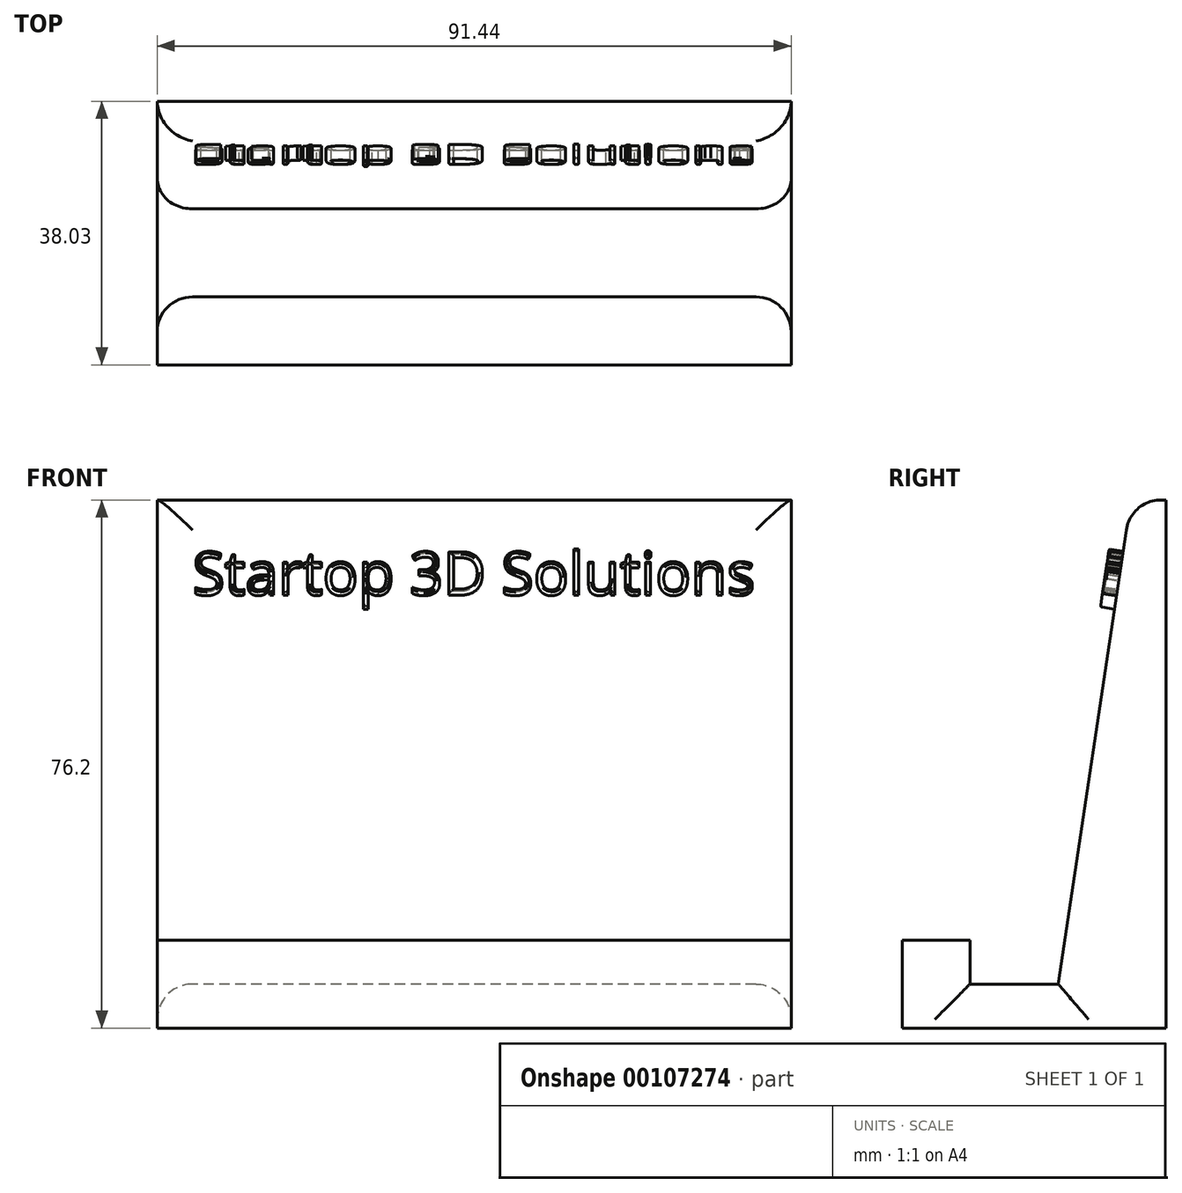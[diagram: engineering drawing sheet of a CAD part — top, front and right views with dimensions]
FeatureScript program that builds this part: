
annotation { "Feature Type Name" : "Feature", "Feature Type Description" : "" }
export const myFeature = defineFeature(function(context is Context, id is Id, definition is map)
    precondition{}
    {
        {
            var Q0;
            Q0=qCreatedBy(makeId("Right.planeOp"),FACE);
            var sketch = newSketch(context, id + "F0", { "sketchPlane" : qUnion([Q0])});
            skLineSegment(sketch, "E0", {"start": v(0, 0) * mm, "end": v(38.03, 0) * mm});
            skLineSegment(sketch, "E1", {"start": v(38.03, 0) * mm, "end": v(38.03, 76.2) * mm});
            skLineSegment(sketch, "E2", {"start": v(38.03, 76.2) * mm, "end": v(32.95, 76.2) * mm});
            skLineSegment(sketch, "E3", {"start": v(32.95, 76.2) * mm, "end": v(22.5, 6.35) * mm});
            skLineSegment(sketch, "E4", {"start": v(22.5, 6.35) * mm, "end": v(9.8, 6.35) * mm});
            skLineSegment(sketch, "E5", {"start": v(9.8, 6.35) * mm, "end": v(9.8, 12.7) * mm});
            skLineSegment(sketch, "E6", {"start": v(9.8, 12.7) * mm, "end": v(0, 12.7) * mm});
            skLineSegment(sketch, "E7", {"start": v(0, 12.7) * mm, "end": v(0, 0) * mm});
            skSolve(sketch);
        }
        {
            var Q0;
            Q0=makeQuery(id+"F0.imprint","IMPRINT",FACE,{"disambiguationData":[TD([[makeQuery(id+"F0.imprint","IMPRINT",EDGE,{"derivedFrom":sQuery(id+"F0.wireOp",EDGE,"E0")}),1.0]])]});
            extrude(context, id + "F1", {"entities" : qUnion([Q0]), "depth" : 91.44 * mm});
        }
        {
            var Q0;
            Q0=makeQuery(id+"F1.opExtrude","SWEPT_EDGE",EDGE,{"disambiguationData":[OSD([sQuery(id+"F0.wireOp",EDGE,"E2"),sQuery(id+"F0.wireOp",EDGE,"E3")])]});
            var Q1;
            Q1=makeQuery(id+"F1.opExtrude","CAP_EDGE",EDGE,{"disambiguationData":[OSD([sQuery(id+"F0.wireOp",EDGE,"E3")])],"isStart":false});
            var Q2;
            Q2=makeQuery(id+"F1.opExtrude","CAP_EDGE",EDGE,{"disambiguationData":[OSD([sQuery(id+"F0.wireOp",EDGE,"E3")])],"isStart":true});
            var Q3;
            Q3=makeQuery(id+"F1.opExtrude","CAP_EDGE",EDGE,{"disambiguationData":[OSD([sQuery(id+"F0.wireOp",EDGE,"E4")])],"isStart":false});
            var Q4;
            Q4=makeQuery(id+"F1.opExtrude","CAP_EDGE",EDGE,{"disambiguationData":[OSD([sQuery(id+"F0.wireOp",EDGE,"E4")])],"isStart":true});
            var Q5;
            Q5=makeQuery(id+"F1.opExtrude","CAP_EDGE",EDGE,{"disambiguationData":[OSD([sQuery(id+"F0.wireOp",EDGE,"E5")])],"isStart":true});
            var Q6;
            Q6=makeQuery(id+"F1.opExtrude","CAP_EDGE",EDGE,{"disambiguationData":[OSD([sQuery(id+"F0.wireOp",EDGE,"E5")])],"isStart":false});
            fillet(context, id + "F2", {"entities" : qUnion([Q0, Q1, Q2, Q3, Q4, Q5, Q6]), "radius" : 5.08 * mm, "tangentPropagation" : true, "allowEdgeOverflow" : false});
        }
        {
            var Q0;
            Q0=makeQuery(id+"F1.opExtrude","SWEPT_FACE",FACE,{"disambiguationData":[OSD([sQuery(id+"F0.wireOp",EDGE,"E3")])]});
            var sketch = newSketch(context, id + "F3", { "sketchPlane" : qUnion([Q0])});
            skText(sketch, "E8", { "text": "Startop 3D Solutions", "fontName": "OpenSans-Regular.ttf"});
            const initialGuessF3  = {"E8": [0.00508, 0.06635, 1, 0, 0.0061]};
            skSetInitialGuess(sketch, initialGuessF3);
            skSolve(sketch);
        }
        {
            var Q0;
            Q0=qSketchRegion(id+"F3",true);
            extrude(context, id + "F4", {"entities" : qUnion([Q0]), "operationType" : NewBodyOperationType.ADD, "depth" : 2.03 * mm});
        }
        {
            var Q0;
            Q0=makeQuery(id+"F4.opExtrude","CAP_FACE",FACE,{"disambiguationData":[OSD([sQuery(id+"F3.wireOp",EDGE,"E8.sketch_text.stroke-0"),sQuery(id+"F3.wireOp",EDGE,"E8.sketch_text.stroke-1"),sQuery(id+"F3.wireOp",EDGE,"E8.sketch_text.stroke-2"),sQuery(id+"F3.wireOp",EDGE,"E8.sketch_text.stroke-3"),sQuery(id+"F3.wireOp",EDGE,"E8.sketch_text.stroke-4"),sQuery(id+"F3.wireOp",EDGE,"E8.sketch_text.stroke-5"),sQuery(id+"F3.wireOp",EDGE,"E8.sketch_text.stroke-6"),sQuery(id+"F3.wireOp",EDGE,"E8.sketch_text.stroke-7"),sQuery(id+"F3.wireOp",EDGE,"E8.sketch_text.stroke-8"),sQuery(id+"F3.wireOp",EDGE,"E8.sketch_text.stroke-9"),sQuery(id+"F3.wireOp",EDGE,"E8.sketch_text.stroke-10"),sQuery(id+"F3.wireOp",EDGE,"E8.sketch_text.stroke-11"),sQuery(id+"F3.wireOp",EDGE,"E8.sketch_text.stroke-12"),sQuery(id+"F3.wireOp",EDGE,"E8.sketch_text.stroke-13"),sQuery(id+"F3.wireOp",EDGE,"E8.sketch_text.stroke-14"),sQuery(id+"F3.wireOp",EDGE,"E8.sketch_text.stroke-15"),sQuery(id+"F3.wireOp",EDGE,"E8.sketch_text.stroke-16"),sQuery(id+"F3.wireOp",EDGE,"E8.sketch_text.stroke-17"),sQuery(id+"F3.wireOp",EDGE,"E8.sketch_text.stroke-18"),sQuery(id+"F3.wireOp",EDGE,"E8.sketch_text.stroke-19"),sQuery(id+"F3.wireOp",EDGE,"E8.sketch_text.stroke-20"),sQuery(id+"F3.wireOp",EDGE,"E8.sketch_text.stroke-21"),sQuery(id+"F3.wireOp",EDGE,"E8.sketch_text.stroke-22"),sQuery(id+"F3.wireOp",EDGE,"E8.sketch_text.stroke-23"),sQuery(id+"F3.wireOp",EDGE,"E8.sketch_text.stroke-24")])],"isStart":false});
            var Q1;
            Q1=makeQuery(id+"F4.opExtrude","CAP_FACE",FACE,{"disambiguationData":[OSD([sQuery(id+"F3.wireOp",EDGE,"E8.sketch_text.stroke-25"),sQuery(id+"F3.wireOp",EDGE,"E8.sketch_text.stroke-26"),sQuery(id+"F3.wireOp",EDGE,"E8.sketch_text.stroke-27"),sQuery(id+"F3.wireOp",EDGE,"E8.sketch_text.stroke-28"),sQuery(id+"F3.wireOp",EDGE,"E8.sketch_text.stroke-29"),sQuery(id+"F3.wireOp",EDGE,"E8.sketch_text.stroke-30"),sQuery(id+"F3.wireOp",EDGE,"E8.sketch_text.stroke-31"),sQuery(id+"F3.wireOp",EDGE,"E8.sketch_text.stroke-32"),sQuery(id+"F3.wireOp",EDGE,"E8.sketch_text.stroke-33"),sQuery(id+"F3.wireOp",EDGE,"E8.sketch_text.stroke-34"),sQuery(id+"F3.wireOp",EDGE,"E8.sketch_text.stroke-35"),sQuery(id+"F3.wireOp",EDGE,"E8.sketch_text.stroke-36"),sQuery(id+"F3.wireOp",EDGE,"E8.sketch_text.stroke-37"),sQuery(id+"F3.wireOp",EDGE,"E8.sketch_text.stroke-38"),sQuery(id+"F3.wireOp",EDGE,"E8.sketch_text.stroke-39"),sQuery(id+"F3.wireOp",EDGE,"E8.sketch_text.stroke-40"),sQuery(id+"F3.wireOp",EDGE,"E8.sketch_text.stroke-41"),sQuery(id+"F3.wireOp",EDGE,"E8.sketch_text.stroke-42"),sQuery(id+"F3.wireOp",EDGE,"E8.sketch_text.stroke-43")])],"isStart":false});
            var Q2;
            Q2=makeQuery(id+"F4.opExtrude","CAP_FACE",FACE,{"disambiguationData":[OSD([sQuery(id+"F3.wireOp",EDGE,"E8.sketch_text.stroke-44"),sQuery(id+"F3.wireOp",EDGE,"E8.sketch_text.stroke-45"),sQuery(id+"F3.wireOp",EDGE,"E8.sketch_text.stroke-46"),sQuery(id+"F3.wireOp",EDGE,"E8.sketch_text.stroke-47"),sQuery(id+"F3.wireOp",EDGE,"E8.sketch_text.stroke-48"),sQuery(id+"F3.wireOp",EDGE,"E8.sketch_text.stroke-49"),sQuery(id+"F3.wireOp",EDGE,"E8.sketch_text.stroke-50"),sQuery(id+"F3.wireOp",EDGE,"E8.sketch_text.stroke-51"),sQuery(id+"F3.wireOp",EDGE,"E8.sketch_text.stroke-52"),sQuery(id+"F3.wireOp",EDGE,"E8.sketch_text.stroke-53"),sQuery(id+"F3.wireOp",EDGE,"E8.sketch_text.stroke-54"),sQuery(id+"F3.wireOp",EDGE,"E8.sketch_text.stroke-55"),sQuery(id+"F3.wireOp",EDGE,"E8.sketch_text.stroke-56"),sQuery(id+"F3.wireOp",EDGE,"E8.sketch_text.stroke-57"),sQuery(id+"F3.wireOp",EDGE,"E8.sketch_text.stroke-58"),sQuery(id+"F3.wireOp",EDGE,"E8.sketch_text.stroke-59"),sQuery(id+"F3.wireOp",EDGE,"E8.sketch_text.stroke-60"),sQuery(id+"F3.wireOp",EDGE,"E8.sketch_text.stroke-61"),sQuery(id+"F3.wireOp",EDGE,"E8.sketch_text.stroke-62"),sQuery(id+"F3.wireOp",EDGE,"E8.sketch_text.stroke-63"),sQuery(id+"F3.wireOp",EDGE,"E8.sketch_text.stroke-64"),sQuery(id+"F3.wireOp",EDGE,"E8.sketch_text.stroke-65"),sQuery(id+"F3.wireOp",EDGE,"E8.sketch_text.stroke-66"),sQuery(id+"F3.wireOp",EDGE,"E8.sketch_text.stroke-67"),sQuery(id+"F3.wireOp",EDGE,"E8.sketch_text.stroke-68"),sQuery(id+"F3.wireOp",EDGE,"E8.sketch_text.stroke-69"),sQuery(id+"F3.wireOp",EDGE,"E8.sketch_text.stroke-70")])],"isStart":false});
            var Q3;
            Q3=makeQuery(id+"F4.opExtrude","CAP_FACE",FACE,{"disambiguationData":[OSD([sQuery(id+"F3.wireOp",EDGE,"E8.sketch_text.stroke-71"),sQuery(id+"F3.wireOp",EDGE,"E8.sketch_text.stroke-72"),sQuery(id+"F3.wireOp",EDGE,"E8.sketch_text.stroke-73"),sQuery(id+"F3.wireOp",EDGE,"E8.sketch_text.stroke-74"),sQuery(id+"F3.wireOp",EDGE,"E8.sketch_text.stroke-75"),sQuery(id+"F3.wireOp",EDGE,"E8.sketch_text.stroke-76"),sQuery(id+"F3.wireOp",EDGE,"E8.sketch_text.stroke-77"),sQuery(id+"F3.wireOp",EDGE,"E8.sketch_text.stroke-78"),sQuery(id+"F3.wireOp",EDGE,"E8.sketch_text.stroke-79"),sQuery(id+"F3.wireOp",EDGE,"E8.sketch_text.stroke-80"),sQuery(id+"F3.wireOp",EDGE,"E8.sketch_text.stroke-81"),sQuery(id+"F3.wireOp",EDGE,"E8.sketch_text.stroke-82"),sQuery(id+"F3.wireOp",EDGE,"E8.sketch_text.stroke-83")])],"isStart":false});
            var Q4;
            Q4=makeQuery(id+"F4.opExtrude","CAP_FACE",FACE,{"disambiguationData":[OSD([sQuery(id+"F3.wireOp",EDGE,"E8.sketch_text.stroke-84"),sQuery(id+"F3.wireOp",EDGE,"E8.sketch_text.stroke-85"),sQuery(id+"F3.wireOp",EDGE,"E8.sketch_text.stroke-86"),sQuery(id+"F3.wireOp",EDGE,"E8.sketch_text.stroke-87"),sQuery(id+"F3.wireOp",EDGE,"E8.sketch_text.stroke-88"),sQuery(id+"F3.wireOp",EDGE,"E8.sketch_text.stroke-89"),sQuery(id+"F3.wireOp",EDGE,"E8.sketch_text.stroke-90"),sQuery(id+"F3.wireOp",EDGE,"E8.sketch_text.stroke-91"),sQuery(id+"F3.wireOp",EDGE,"E8.sketch_text.stroke-92"),sQuery(id+"F3.wireOp",EDGE,"E8.sketch_text.stroke-93"),sQuery(id+"F3.wireOp",EDGE,"E8.sketch_text.stroke-94"),sQuery(id+"F3.wireOp",EDGE,"E8.sketch_text.stroke-95"),sQuery(id+"F3.wireOp",EDGE,"E8.sketch_text.stroke-96"),sQuery(id+"F3.wireOp",EDGE,"E8.sketch_text.stroke-97"),sQuery(id+"F3.wireOp",EDGE,"E8.sketch_text.stroke-98"),sQuery(id+"F3.wireOp",EDGE,"E8.sketch_text.stroke-99"),sQuery(id+"F3.wireOp",EDGE,"E8.sketch_text.stroke-100"),sQuery(id+"F3.wireOp",EDGE,"E8.sketch_text.stroke-101"),sQuery(id+"F3.wireOp",EDGE,"E8.sketch_text.stroke-102")])],"isStart":false});
            var Q5;
            Q5=makeQuery(id+"F4.opExtrude","CAP_FACE",FACE,{"disambiguationData":[OSD([sQuery(id+"F3.wireOp",EDGE,"E8.sketch_text.stroke-103"),sQuery(id+"F3.wireOp",EDGE,"E8.sketch_text.stroke-104"),sQuery(id+"F3.wireOp",EDGE,"E8.sketch_text.stroke-105"),sQuery(id+"F3.wireOp",EDGE,"E8.sketch_text.stroke-106"),sQuery(id+"F3.wireOp",EDGE,"E8.sketch_text.stroke-107"),sQuery(id+"F3.wireOp",EDGE,"E8.sketch_text.stroke-108"),sQuery(id+"F3.wireOp",EDGE,"E8.sketch_text.stroke-109"),sQuery(id+"F3.wireOp",EDGE,"E8.sketch_text.stroke-110"),sQuery(id+"F3.wireOp",EDGE,"E8.sketch_text.stroke-111"),sQuery(id+"F3.wireOp",EDGE,"E8.sketch_text.stroke-112"),sQuery(id+"F3.wireOp",EDGE,"E8.sketch_text.stroke-113"),sQuery(id+"F3.wireOp",EDGE,"E8.sketch_text.stroke-114"),sQuery(id+"F3.wireOp",EDGE,"E8.sketch_text.stroke-115"),sQuery(id+"F3.wireOp",EDGE,"E8.sketch_text.stroke-116"),sQuery(id+"F3.wireOp",EDGE,"E8.sketch_text.stroke-117"),sQuery(id+"F3.wireOp",EDGE,"E8.sketch_text.stroke-118"),sQuery(id+"F3.wireOp",EDGE,"E8.sketch_text.stroke-119")])],"isStart":false});
            var Q6;
            Q6=makeQuery(id+"F4.opExtrude","CAP_FACE",FACE,{"disambiguationData":[OSD([sQuery(id+"F3.wireOp",EDGE,"E8.sketch_text.stroke-120"),sQuery(id+"F3.wireOp",EDGE,"E8.sketch_text.stroke-121"),sQuery(id+"F3.wireOp",EDGE,"E8.sketch_text.stroke-122"),sQuery(id+"F3.wireOp",EDGE,"E8.sketch_text.stroke-123"),sQuery(id+"F3.wireOp",EDGE,"E8.sketch_text.stroke-124"),sQuery(id+"F3.wireOp",EDGE,"E8.sketch_text.stroke-125"),sQuery(id+"F3.wireOp",EDGE,"E8.sketch_text.stroke-126"),sQuery(id+"F3.wireOp",EDGE,"E8.sketch_text.stroke-127"),sQuery(id+"F3.wireOp",EDGE,"E8.sketch_text.stroke-128"),sQuery(id+"F3.wireOp",EDGE,"E8.sketch_text.stroke-129"),sQuery(id+"F3.wireOp",EDGE,"E8.sketch_text.stroke-130"),sQuery(id+"F3.wireOp",EDGE,"E8.sketch_text.stroke-131"),sQuery(id+"F3.wireOp",EDGE,"E8.sketch_text.stroke-132"),sQuery(id+"F3.wireOp",EDGE,"E8.sketch_text.stroke-133"),sQuery(id+"F3.wireOp",EDGE,"E8.sketch_text.stroke-134"),sQuery(id+"F3.wireOp",EDGE,"E8.sketch_text.stroke-135"),sQuery(id+"F3.wireOp",EDGE,"E8.sketch_text.stroke-136"),sQuery(id+"F3.wireOp",EDGE,"E8.sketch_text.stroke-137"),sQuery(id+"F3.wireOp",EDGE,"E8.sketch_text.stroke-138"),sQuery(id+"F3.wireOp",EDGE,"E8.sketch_text.stroke-139"),sQuery(id+"F3.wireOp",EDGE,"E8.sketch_text.stroke-140"),sQuery(id+"F3.wireOp",EDGE,"E8.sketch_text.stroke-141"),sQuery(id+"F3.wireOp",EDGE,"E8.sketch_text.stroke-142"),sQuery(id+"F3.wireOp",EDGE,"E8.sketch_text.stroke-143"),sQuery(id+"F3.wireOp",EDGE,"E8.sketch_text.stroke-144")])],"isStart":false});
            var Q7;
            Q7=makeQuery(id+"F4.opExtrude","CAP_FACE",FACE,{"disambiguationData":[OSD([sQuery(id+"F3.wireOp",EDGE,"E8.sketch_text.stroke-145"),sQuery(id+"F3.wireOp",EDGE,"E8.sketch_text.stroke-146"),sQuery(id+"F3.wireOp",EDGE,"E8.sketch_text.stroke-147"),sQuery(id+"F3.wireOp",EDGE,"E8.sketch_text.stroke-148"),sQuery(id+"F3.wireOp",EDGE,"E8.sketch_text.stroke-149"),sQuery(id+"F3.wireOp",EDGE,"E8.sketch_text.stroke-150"),sQuery(id+"F3.wireOp",EDGE,"E8.sketch_text.stroke-151"),sQuery(id+"F3.wireOp",EDGE,"E8.sketch_text.stroke-152"),sQuery(id+"F3.wireOp",EDGE,"E8.sketch_text.stroke-153"),sQuery(id+"F3.wireOp",EDGE,"E8.sketch_text.stroke-154"),sQuery(id+"F3.wireOp",EDGE,"E8.sketch_text.stroke-155"),sQuery(id+"F3.wireOp",EDGE,"E8.sketch_text.stroke-156"),sQuery(id+"F3.wireOp",EDGE,"E8.sketch_text.stroke-157"),sQuery(id+"F3.wireOp",EDGE,"E8.sketch_text.stroke-158"),sQuery(id+"F3.wireOp",EDGE,"E8.sketch_text.stroke-159"),sQuery(id+"F3.wireOp",EDGE,"E8.sketch_text.stroke-160"),sQuery(id+"F3.wireOp",EDGE,"E8.sketch_text.stroke-161"),sQuery(id+"F3.wireOp",EDGE,"E8.sketch_text.stroke-162"),sQuery(id+"F3.wireOp",EDGE,"E8.sketch_text.stroke-163"),sQuery(id+"F3.wireOp",EDGE,"E8.sketch_text.stroke-164"),sQuery(id+"F3.wireOp",EDGE,"E8.sketch_text.stroke-165"),sQuery(id+"F3.wireOp",EDGE,"E8.sketch_text.stroke-166"),sQuery(id+"F3.wireOp",EDGE,"E8.sketch_text.stroke-167"),sQuery(id+"F3.wireOp",EDGE,"E8.sketch_text.stroke-168"),sQuery(id+"F3.wireOp",EDGE,"E8.sketch_text.stroke-169"),sQuery(id+"F3.wireOp",EDGE,"E8.sketch_text.stroke-170"),sQuery(id+"F3.wireOp",EDGE,"E8.sketch_text.stroke-171"),sQuery(id+"F3.wireOp",EDGE,"E8.sketch_text.stroke-172")])],"isStart":false});
            var Q8;
            Q8=makeQuery(id+"F4.opExtrude","CAP_FACE",FACE,{"disambiguationData":[OSD([sQuery(id+"F3.wireOp",EDGE,"E8.sketch_text.stroke-173"),sQuery(id+"F3.wireOp",EDGE,"E8.sketch_text.stroke-174"),sQuery(id+"F3.wireOp",EDGE,"E8.sketch_text.stroke-175"),sQuery(id+"F3.wireOp",EDGE,"E8.sketch_text.stroke-176"),sQuery(id+"F3.wireOp",EDGE,"E8.sketch_text.stroke-177"),sQuery(id+"F3.wireOp",EDGE,"E8.sketch_text.stroke-178"),sQuery(id+"F3.wireOp",EDGE,"E8.sketch_text.stroke-179"),sQuery(id+"F3.wireOp",EDGE,"E8.sketch_text.stroke-180"),sQuery(id+"F3.wireOp",EDGE,"E8.sketch_text.stroke-181"),sQuery(id+"F3.wireOp",EDGE,"E8.sketch_text.stroke-182"),sQuery(id+"F3.wireOp",EDGE,"E8.sketch_text.stroke-183"),sQuery(id+"F3.wireOp",EDGE,"E8.sketch_text.stroke-184"),sQuery(id+"F3.wireOp",EDGE,"E8.sketch_text.stroke-185"),sQuery(id+"F3.wireOp",EDGE,"E8.sketch_text.stroke-186")])],"isStart":false});
            fillet(context, id + "F5", {"entities" : qUnion([Q0, Q1, Q2, Q3, Q4, Q5, Q6, Q7, Q8]), "radius" : 0.25 * mm, "tangentPropagation" : true, "allowEdgeOverflow" : false});
        }
        {
            var Q0;
            Q0=makeQuery(id+"F4.opExtrude","CAP_FACE",FACE,{"disambiguationData":[OSD([sQuery(id+"F3.wireOp",EDGE,"E8.sketch_text.stroke-212"),sQuery(id+"F3.wireOp",EDGE,"E8.sketch_text.stroke-213"),sQuery(id+"F3.wireOp",EDGE,"E8.sketch_text.stroke-214"),sQuery(id+"F3.wireOp",EDGE,"E8.sketch_text.stroke-215"),sQuery(id+"F3.wireOp",EDGE,"E8.sketch_text.stroke-216"),sQuery(id+"F3.wireOp",EDGE,"E8.sketch_text.stroke-217"),sQuery(id+"F3.wireOp",EDGE,"E8.sketch_text.stroke-218"),sQuery(id+"F3.wireOp",EDGE,"E8.sketch_text.stroke-219"),sQuery(id+"F3.wireOp",EDGE,"E8.sketch_text.stroke-220"),sQuery(id+"F3.wireOp",EDGE,"E8.sketch_text.stroke-221"),sQuery(id+"F3.wireOp",EDGE,"E8.sketch_text.stroke-222"),sQuery(id+"F3.wireOp",EDGE,"E8.sketch_text.stroke-223"),sQuery(id+"F3.wireOp",EDGE,"E8.sketch_text.stroke-224"),sQuery(id+"F3.wireOp",EDGE,"E8.sketch_text.stroke-225"),sQuery(id+"F3.wireOp",EDGE,"E8.sketch_text.stroke-226"),sQuery(id+"F3.wireOp",EDGE,"E8.sketch_text.stroke-227"),sQuery(id+"F3.wireOp",EDGE,"E8.sketch_text.stroke-228")])],"isStart":false});
            var Q1;
            Q1=makeQuery(id+"F4.opExtrude","CAP_FACE",FACE,{"disambiguationData":[OSD([sQuery(id+"F3.wireOp",EDGE,"E8.sketch_text.stroke-229"),sQuery(id+"F3.wireOp",EDGE,"E8.sketch_text.stroke-230"),sQuery(id+"F3.wireOp",EDGE,"E8.sketch_text.stroke-231"),sQuery(id+"F3.wireOp",EDGE,"E8.sketch_text.stroke-232")])],"isStart":false});
            var Q2;
            Q2=makeQuery(id+"F4.opExtrude","CAP_FACE",FACE,{"disambiguationData":[OSD([sQuery(id+"F3.wireOp",EDGE,"E8.sketch_text.stroke-233"),sQuery(id+"F3.wireOp",EDGE,"E8.sketch_text.stroke-234"),sQuery(id+"F3.wireOp",EDGE,"E8.sketch_text.stroke-235"),sQuery(id+"F3.wireOp",EDGE,"E8.sketch_text.stroke-236"),sQuery(id+"F3.wireOp",EDGE,"E8.sketch_text.stroke-237"),sQuery(id+"F3.wireOp",EDGE,"E8.sketch_text.stroke-238"),sQuery(id+"F3.wireOp",EDGE,"E8.sketch_text.stroke-239"),sQuery(id+"F3.wireOp",EDGE,"E8.sketch_text.stroke-240"),sQuery(id+"F3.wireOp",EDGE,"E8.sketch_text.stroke-241"),sQuery(id+"F3.wireOp",EDGE,"E8.sketch_text.stroke-242"),sQuery(id+"F3.wireOp",EDGE,"E8.sketch_text.stroke-243"),sQuery(id+"F3.wireOp",EDGE,"E8.sketch_text.stroke-244"),sQuery(id+"F3.wireOp",EDGE,"E8.sketch_text.stroke-245"),sQuery(id+"F3.wireOp",EDGE,"E8.sketch_text.stroke-246"),sQuery(id+"F3.wireOp",EDGE,"E8.sketch_text.stroke-247"),sQuery(id+"F3.wireOp",EDGE,"E8.sketch_text.stroke-248"),sQuery(id+"F3.wireOp",EDGE,"E8.sketch_text.stroke-249")])],"isStart":false});
            var Q3;
            Q3=makeQuery(id+"F4.opExtrude","CAP_FACE",FACE,{"disambiguationData":[OSD([sQuery(id+"F3.wireOp",EDGE,"E8.sketch_text.stroke-250"),sQuery(id+"F3.wireOp",EDGE,"E8.sketch_text.stroke-251"),sQuery(id+"F3.wireOp",EDGE,"E8.sketch_text.stroke-252"),sQuery(id+"F3.wireOp",EDGE,"E8.sketch_text.stroke-253"),sQuery(id+"F3.wireOp",EDGE,"E8.sketch_text.stroke-254"),sQuery(id+"F3.wireOp",EDGE,"E8.sketch_text.stroke-255"),sQuery(id+"F3.wireOp",EDGE,"E8.sketch_text.stroke-256"),sQuery(id+"F3.wireOp",EDGE,"E8.sketch_text.stroke-257"),sQuery(id+"F3.wireOp",EDGE,"E8.sketch_text.stroke-258"),sQuery(id+"F3.wireOp",EDGE,"E8.sketch_text.stroke-259"),sQuery(id+"F3.wireOp",EDGE,"E8.sketch_text.stroke-260"),sQuery(id+"F3.wireOp",EDGE,"E8.sketch_text.stroke-261"),sQuery(id+"F3.wireOp",EDGE,"E8.sketch_text.stroke-262"),sQuery(id+"F3.wireOp",EDGE,"E8.sketch_text.stroke-263"),sQuery(id+"F3.wireOp",EDGE,"E8.sketch_text.stroke-264"),sQuery(id+"F3.wireOp",EDGE,"E8.sketch_text.stroke-265"),sQuery(id+"F3.wireOp",EDGE,"E8.sketch_text.stroke-266"),sQuery(id+"F3.wireOp",EDGE,"E8.sketch_text.stroke-267"),sQuery(id+"F3.wireOp",EDGE,"E8.sketch_text.stroke-268")])],"isStart":false});
            var Q4;
            Q4=makeQuery(id+"F4.opExtrude","CAP_FACE",FACE,{"disambiguationData":[OSD([sQuery(id+"F3.wireOp",EDGE,"E8.sketch_text.stroke-269"),sQuery(id+"F3.wireOp",EDGE,"E8.sketch_text.stroke-270"),sQuery(id+"F3.wireOp",EDGE,"E8.sketch_text.stroke-271"),sQuery(id+"F3.wireOp",EDGE,"E8.sketch_text.stroke-272")])],"isStart":false});
            var Q5;
            Q5=makeQuery(id+"F4.opExtrude","CAP_FACE",FACE,{"disambiguationData":[OSD([sQuery(id+"F3.wireOp",EDGE,"E8.sketch_text.stroke-187"),sQuery(id+"F3.wireOp",EDGE,"E8.sketch_text.stroke-188"),sQuery(id+"F3.wireOp",EDGE,"E8.sketch_text.stroke-189"),sQuery(id+"F3.wireOp",EDGE,"E8.sketch_text.stroke-190"),sQuery(id+"F3.wireOp",EDGE,"E8.sketch_text.stroke-191"),sQuery(id+"F3.wireOp",EDGE,"E8.sketch_text.stroke-192"),sQuery(id+"F3.wireOp",EDGE,"E8.sketch_text.stroke-193"),sQuery(id+"F3.wireOp",EDGE,"E8.sketch_text.stroke-194"),sQuery(id+"F3.wireOp",EDGE,"E8.sketch_text.stroke-195"),sQuery(id+"F3.wireOp",EDGE,"E8.sketch_text.stroke-196"),sQuery(id+"F3.wireOp",EDGE,"E8.sketch_text.stroke-197"),sQuery(id+"F3.wireOp",EDGE,"E8.sketch_text.stroke-198"),sQuery(id+"F3.wireOp",EDGE,"E8.sketch_text.stroke-199"),sQuery(id+"F3.wireOp",EDGE,"E8.sketch_text.stroke-200"),sQuery(id+"F3.wireOp",EDGE,"E8.sketch_text.stroke-201"),sQuery(id+"F3.wireOp",EDGE,"E8.sketch_text.stroke-202"),sQuery(id+"F3.wireOp",EDGE,"E8.sketch_text.stroke-203"),sQuery(id+"F3.wireOp",EDGE,"E8.sketch_text.stroke-204"),sQuery(id+"F3.wireOp",EDGE,"E8.sketch_text.stroke-205"),sQuery(id+"F3.wireOp",EDGE,"E8.sketch_text.stroke-206"),sQuery(id+"F3.wireOp",EDGE,"E8.sketch_text.stroke-207"),sQuery(id+"F3.wireOp",EDGE,"E8.sketch_text.stroke-208"),sQuery(id+"F3.wireOp",EDGE,"E8.sketch_text.stroke-209"),sQuery(id+"F3.wireOp",EDGE,"E8.sketch_text.stroke-210"),sQuery(id+"F3.wireOp",EDGE,"E8.sketch_text.stroke-211")])],"isStart":false});
            var Q6;
            Q6=makeQuery(id+"F4.opExtrude","CAP_FACE",FACE,{"disambiguationData":[OSD([sQuery(id+"F3.wireOp",EDGE,"E8.sketch_text.stroke-273"),sQuery(id+"F3.wireOp",EDGE,"E8.sketch_text.stroke-274"),sQuery(id+"F3.wireOp",EDGE,"E8.sketch_text.stroke-275"),sQuery(id+"F3.wireOp",EDGE,"E8.sketch_text.stroke-276"),sQuery(id+"F3.wireOp",EDGE,"E8.sketch_text.stroke-277"),sQuery(id+"F3.wireOp",EDGE,"E8.sketch_text.stroke-278"),sQuery(id+"F3.wireOp",EDGE,"E8.sketch_text.stroke-279"),sQuery(id+"F3.wireOp",EDGE,"E8.sketch_text.stroke-280")])],"isStart":false});
            var Q7;
            Q7=makeQuery(id+"F4.opExtrude","CAP_FACE",FACE,{"disambiguationData":[OSD([sQuery(id+"F3.wireOp",EDGE,"E8.sketch_text.stroke-281"),sQuery(id+"F3.wireOp",EDGE,"E8.sketch_text.stroke-282"),sQuery(id+"F3.wireOp",EDGE,"E8.sketch_text.stroke-283"),sQuery(id+"F3.wireOp",EDGE,"E8.sketch_text.stroke-284"),sQuery(id+"F3.wireOp",EDGE,"E8.sketch_text.stroke-285"),sQuery(id+"F3.wireOp",EDGE,"E8.sketch_text.stroke-286"),sQuery(id+"F3.wireOp",EDGE,"E8.sketch_text.stroke-287"),sQuery(id+"F3.wireOp",EDGE,"E8.sketch_text.stroke-288"),sQuery(id+"F3.wireOp",EDGE,"E8.sketch_text.stroke-289"),sQuery(id+"F3.wireOp",EDGE,"E8.sketch_text.stroke-290"),sQuery(id+"F3.wireOp",EDGE,"E8.sketch_text.stroke-291"),sQuery(id+"F3.wireOp",EDGE,"E8.sketch_text.stroke-292"),sQuery(id+"F3.wireOp",EDGE,"E8.sketch_text.stroke-293"),sQuery(id+"F3.wireOp",EDGE,"E8.sketch_text.stroke-294"),sQuery(id+"F3.wireOp",EDGE,"E8.sketch_text.stroke-295"),sQuery(id+"F3.wireOp",EDGE,"E8.sketch_text.stroke-296"),sQuery(id+"F3.wireOp",EDGE,"E8.sketch_text.stroke-297")])],"isStart":false});
            var Q8;
            Q8=makeQuery(id+"F4.opExtrude","CAP_FACE",FACE,{"disambiguationData":[OSD([sQuery(id+"F3.wireOp",EDGE,"E8.sketch_text.stroke-298"),sQuery(id+"F3.wireOp",EDGE,"E8.sketch_text.stroke-299"),sQuery(id+"F3.wireOp",EDGE,"E8.sketch_text.stroke-300"),sQuery(id+"F3.wireOp",EDGE,"E8.sketch_text.stroke-301"),sQuery(id+"F3.wireOp",EDGE,"E8.sketch_text.stroke-302"),sQuery(id+"F3.wireOp",EDGE,"E8.sketch_text.stroke-303"),sQuery(id+"F3.wireOp",EDGE,"E8.sketch_text.stroke-304"),sQuery(id+"F3.wireOp",EDGE,"E8.sketch_text.stroke-305"),sQuery(id+"F3.wireOp",EDGE,"E8.sketch_text.stroke-306"),sQuery(id+"F3.wireOp",EDGE,"E8.sketch_text.stroke-307"),sQuery(id+"F3.wireOp",EDGE,"E8.sketch_text.stroke-308"),sQuery(id+"F3.wireOp",EDGE,"E8.sketch_text.stroke-309"),sQuery(id+"F3.wireOp",EDGE,"E8.sketch_text.stroke-310"),sQuery(id+"F3.wireOp",EDGE,"E8.sketch_text.stroke-311"),sQuery(id+"F3.wireOp",EDGE,"E8.sketch_text.stroke-312"),sQuery(id+"F3.wireOp",EDGE,"E8.sketch_text.stroke-313"),sQuery(id+"F3.wireOp",EDGE,"E8.sketch_text.stroke-314")])],"isStart":false});
            var Q9;
            Q9=makeQuery(id+"F4.opExtrude","CAP_FACE",FACE,{"disambiguationData":[OSD([sQuery(id+"F3.wireOp",EDGE,"E8.sketch_text.stroke-315"),sQuery(id+"F3.wireOp",EDGE,"E8.sketch_text.stroke-316"),sQuery(id+"F3.wireOp",EDGE,"E8.sketch_text.stroke-317"),sQuery(id+"F3.wireOp",EDGE,"E8.sketch_text.stroke-318"),sQuery(id+"F3.wireOp",EDGE,"E8.sketch_text.stroke-319"),sQuery(id+"F3.wireOp",EDGE,"E8.sketch_text.stroke-320"),sQuery(id+"F3.wireOp",EDGE,"E8.sketch_text.stroke-321"),sQuery(id+"F3.wireOp",EDGE,"E8.sketch_text.stroke-322"),sQuery(id+"F3.wireOp",EDGE,"E8.sketch_text.stroke-323"),sQuery(id+"F3.wireOp",EDGE,"E8.sketch_text.stroke-324"),sQuery(id+"F3.wireOp",EDGE,"E8.sketch_text.stroke-325"),sQuery(id+"F3.wireOp",EDGE,"E8.sketch_text.stroke-326"),sQuery(id+"F3.wireOp",EDGE,"E8.sketch_text.stroke-327"),sQuery(id+"F3.wireOp",EDGE,"E8.sketch_text.stroke-328"),sQuery(id+"F3.wireOp",EDGE,"E8.sketch_text.stroke-329"),sQuery(id+"F3.wireOp",EDGE,"E8.sketch_text.stroke-330"),sQuery(id+"F3.wireOp",EDGE,"E8.sketch_text.stroke-331"),sQuery(id+"F3.wireOp",EDGE,"E8.sketch_text.stroke-332"),sQuery(id+"F3.wireOp",EDGE,"E8.sketch_text.stroke-333"),sQuery(id+"F3.wireOp",EDGE,"E8.sketch_text.stroke-334"),sQuery(id+"F3.wireOp",EDGE,"E8.sketch_text.stroke-335"),sQuery(id+"F3.wireOp",EDGE,"E8.sketch_text.stroke-336"),sQuery(id+"F3.wireOp",EDGE,"E8.sketch_text.stroke-337"),sQuery(id+"F3.wireOp",EDGE,"E8.sketch_text.stroke-338"),sQuery(id+"F3.wireOp",EDGE,"E8.sketch_text.stroke-339")])],"isStart":false});
            fillet(context, id + "F6", {"entities" : qUnion([Q0, Q1, Q2, Q3, Q4, Q5, Q6, Q7, Q8, Q9]), "radius" : 0.25 * mm, "tangentPropagation" : true, "allowEdgeOverflow" : false});
        }
    });
